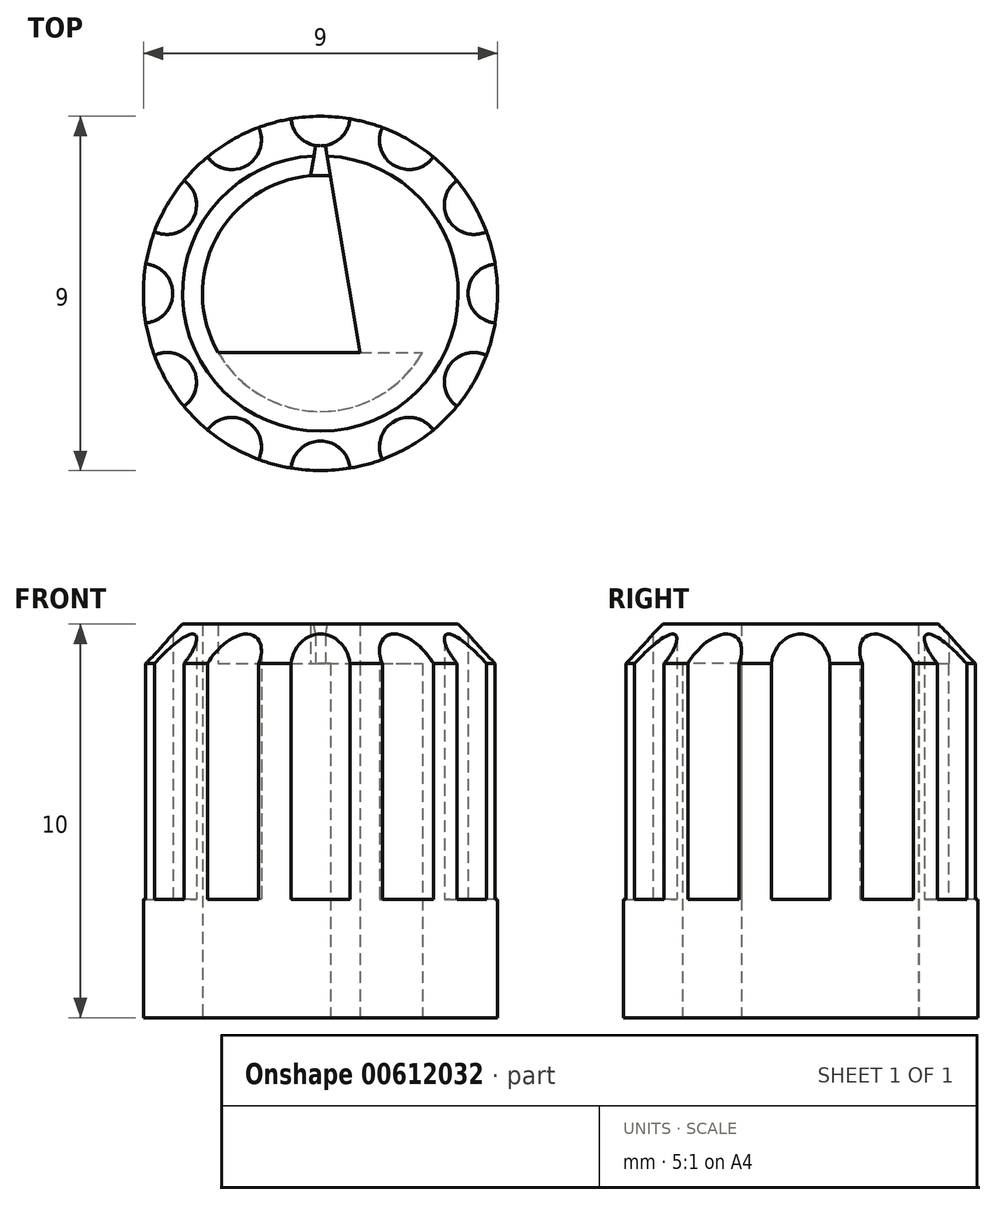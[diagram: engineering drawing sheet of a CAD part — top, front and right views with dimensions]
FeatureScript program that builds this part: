
annotation { "Feature Type Name" : "Feature", "Feature Type Description" : "" }
export const myFeature = defineFeature(function(context is Context, id is Id, definition is map)
    precondition{}
    {
        {
            var Q0;
            Q0=qCreatedBy(makeId("Top.planeOp"),FACE);
            var sketch = newSketch(context, id + "F0", { "sketchPlane" : qUnion([Q0])});
            skCircle(sketch, "E0", {"center": v(0, 0) * mm, "radius": 4.5 * mm});
            skCircle(sketch, "E1", {"center": v(0, 0) * mm, "radius": 3 * mm});
            skLineSegment(sketch, "E2", {"start": v(-2.6, -1.5) * mm, "end": v(2.6, -1.5) * mm});
            skCircle(sketch, "E3", {"center": v(0, 4.5) * mm, "radius": 0.75 * mm});
            skCircle(sketch, "E4.1.0", {"center": v(-2.25, 3.9) * mm, "radius": 0.75 * mm});
            skCircle(sketch, "E4.2.0", {"center": v(-3.9, 2.25) * mm, "radius": 0.75 * mm});
            skCircle(sketch, "E5.1.3.0", {"center": v(-4.5, 0) * mm, "radius": 0.75 * mm});
            skCircle(sketch, "E5.1.4.0", {"center": v(-3.9, -2.25) * mm, "radius": 0.75 * mm});
            skCircle(sketch, "E5.1.5.0", {"center": v(-2.25, -3.9) * mm, "radius": 0.75 * mm});
            skCircle(sketch, "E5.1.6.0", {"center": v(0, -4.5) * mm, "radius": 0.75 * mm});
            skCircle(sketch, "E5.1.7.0", {"center": v(2.25, -3.9) * mm, "radius": 0.75 * mm});
            skCircle(sketch, "E5.1.8.0", {"center": v(3.9, -2.25) * mm, "radius": 0.75 * mm});
            skCircle(sketch, "E5.1.9.0", {"center": v(4.5, 0) * mm, "radius": 0.75 * mm});
            skCircle(sketch, "E5.1.10.0", {"center": v(3.9, 2.25) * mm, "radius": 0.75 * mm});
            skCircle(sketch, "E5.1.11.0", {"center": v(2.25, 3.9) * mm, "radius": 0.75 * mm});
            skLineSegment(sketch, "E6", {"start": v(-1, -1.5) * mm, "end": v(0, 4.5) * mm});
            skLineSegment(sketch, "E7.MirrorCS", {"start": v(1, -1.5) * mm, "end": v(0, 4.5) * mm});
            skSolve(sketch);
        }
        {
            var Q0;
            {var subQ9=sQuery(id+"F0.wireOp",EDGE,"E0");var subQ29=sQuery(id+"F0.wireOp",EDGE,"E5.1.10.0");var subQ30=makeQuery(id+"F0.imprint","INTERSECT",VERTEX,{"disambiguationData":[OD(0.0)],"derivedFrom":[subQ9,subQ29]});Q0=makeQuery(id+"F0.imprint","IMPRINT",FACE,{"disambiguationData":[TD([[makeQuery(id+"F0.imprint","IMPRINT",EDGE,{"disambiguationData":[TD([[subQ30,1.0]])],"derivedFrom":subQ9}),1.0]])]});}
            var Q1;
            {var subQ0=sQuery(id+"F0.wireOp",EDGE,"E2");var subQ1=sQuery(id+"F0.wireOp",EDGE,"E1");var subQ2=makeQuery(id+"F0.imprint","INTERSECT",VERTEX,{"disambiguationData":[OD(0.0)],"derivedFrom":[subQ1,subQ0]});Q1=makeQuery(id+"F0.imprint","IMPRINT",FACE,{"disambiguationData":[TD([[makeQuery(id+"F0.imprint","IMPRINT",EDGE,{"disambiguationData":[TD([[subQ2,-1.0]])],"derivedFrom":subQ1}),1.0]])]});}
            var Q2;
            {var subQ0=sQuery(id+"F0.wireOp",EDGE,"E6");var subQ1=sQuery(id+"F0.wireOp",EDGE,"E1");var subQ2=makeQuery(id+"F0.imprint","INTERSECT",VERTEX,{"derivedFrom":[subQ1,subQ0]});Q2=makeQuery(id+"F0.imprint","IMPRINT",FACE,{"disambiguationData":[TD([[makeQuery(id+"F0.imprint","IMPRINT",EDGE,{"disambiguationData":[TD([[subQ2,1.0]])],"derivedFrom":subQ1}),-1.0]])]});}
            var Q3;
            {var subQ0=sQuery(id+"F0.wireOp",EDGE,"E6");var subQ1=sQuery(id+"F0.wireOp",EDGE,"E3");var subQ2=makeQuery(id+"F0.imprint","INTERSECT",VERTEX,{"derivedFrom":[subQ1,subQ0]});Q3=makeQuery(id+"F0.imprint","IMPRINT",FACE,{"disambiguationData":[TD([[makeQuery(id+"F0.imprint","IMPRINT",EDGE,{"disambiguationData":[TD([[subQ2,-1.0]])],"derivedFrom":subQ1}),1.0]])]});}
            var Q4;
            {var subQ1=sQuery(id+"F0.wireOp",EDGE,"E0");var subQ3=sQuery(id+"F0.wireOp",EDGE,"E3");var subQ4=makeQuery(id+"F0.imprint","INTERSECT",VERTEX,{"disambiguationData":[OD(0.0)],"derivedFrom":[subQ1,subQ3]});Q4=makeQuery(id+"F0.imprint","IMPRINT",FACE,{"disambiguationData":[TD([[makeQuery(id+"F0.imprint","IMPRINT",EDGE,{"disambiguationData":[TD([[subQ4,1.0]])],"derivedFrom":subQ3}),1.0]])]});}
            var Q5;
            {var subQ1=sQuery(id+"F0.wireOp",EDGE,"E0");var subQ3=sQuery(id+"F0.wireOp",EDGE,"E3");var subQ4=makeQuery(id+"F0.imprint","INTERSECT",VERTEX,{"disambiguationData":[OD(1.0)],"derivedFrom":[subQ1,subQ3]});Q5=makeQuery(id+"F0.imprint","IMPRINT",FACE,{"disambiguationData":[TD([[makeQuery(id+"F0.imprint","IMPRINT",EDGE,{"disambiguationData":[TD([[subQ4,-1.0]])],"derivedFrom":subQ3}),1.0]])]});}
            var Q6;
            {var subQ0=sQuery(id+"F0.wireOp",EDGE,"E5.1.11.0");var subQ1=sQuery(id+"F0.wireOp",EDGE,"E0");var subQ2=makeQuery(id+"F0.imprint","INTERSECT",VERTEX,{"disambiguationData":[OD(0.0)],"derivedFrom":[subQ1,subQ0]});Q6=makeQuery(id+"F0.imprint","IMPRINT",FACE,{"disambiguationData":[TD([[makeQuery(id+"F0.imprint","IMPRINT",EDGE,{"disambiguationData":[TD([[subQ2,-1.0]])],"derivedFrom":subQ1}),1.0]])]});}
            var Q7;
            {var subQ0=sQuery(id+"F0.wireOp",EDGE,"E5.1.10.0");var subQ1=sQuery(id+"F0.wireOp",EDGE,"E0");var subQ2=makeQuery(id+"F0.imprint","INTERSECT",VERTEX,{"disambiguationData":[OD(0.0)],"derivedFrom":[subQ1,subQ0]});Q7=makeQuery(id+"F0.imprint","IMPRINT",FACE,{"disambiguationData":[TD([[makeQuery(id+"F0.imprint","IMPRINT",EDGE,{"disambiguationData":[TD([[subQ2,-1.0]])],"derivedFrom":subQ1}),1.0]])]});}
            var Q8;
            {var subQ0=sQuery(id+"F0.wireOp",EDGE,"E5.1.9.0");var subQ1=sQuery(id+"F0.wireOp",EDGE,"E0");var subQ2=makeQuery(id+"F0.imprint","INTERSECT",VERTEX,{"disambiguationData":[OD(0.0)],"derivedFrom":[subQ1,subQ0]});Q8=makeQuery(id+"F0.imprint","IMPRINT",FACE,{"disambiguationData":[TD([[makeQuery(id+"F0.imprint","IMPRINT",EDGE,{"disambiguationData":[TD([[subQ2,1.0]])],"derivedFrom":subQ1}),1.0]])]});}
            var Q9;
            {var subQ0=sQuery(id+"F0.wireOp",EDGE,"E5.1.8.0");var subQ1=sQuery(id+"F0.wireOp",EDGE,"E0");var subQ2=makeQuery(id+"F0.imprint","INTERSECT",VERTEX,{"disambiguationData":[OD(0.0)],"derivedFrom":[subQ1,subQ0]});Q9=makeQuery(id+"F0.imprint","IMPRINT",FACE,{"disambiguationData":[TD([[makeQuery(id+"F0.imprint","IMPRINT",EDGE,{"disambiguationData":[TD([[subQ2,-1.0]])],"derivedFrom":subQ1}),1.0]])]});}
            var Q10;
            {var subQ0=sQuery(id+"F0.wireOp",EDGE,"E5.1.4.0");var subQ1=sQuery(id+"F0.wireOp",EDGE,"E0");var subQ2=makeQuery(id+"F0.imprint","INTERSECT",VERTEX,{"disambiguationData":[OD(0.0)],"derivedFrom":[subQ1,subQ0]});Q10=makeQuery(id+"F0.imprint","IMPRINT",FACE,{"disambiguationData":[TD([[makeQuery(id+"F0.imprint","IMPRINT",EDGE,{"disambiguationData":[TD([[subQ2,-1.0]])],"derivedFrom":subQ1}),1.0]])]});}
            var Q11;
            {var subQ0=sQuery(id+"F0.wireOp",EDGE,"E5.1.3.0");var subQ1=sQuery(id+"F0.wireOp",EDGE,"E0");var subQ2=makeQuery(id+"F0.imprint","INTERSECT",VERTEX,{"disambiguationData":[OD(0.0)],"derivedFrom":[subQ1,subQ0]});Q11=makeQuery(id+"F0.imprint","IMPRINT",FACE,{"disambiguationData":[TD([[makeQuery(id+"F0.imprint","IMPRINT",EDGE,{"disambiguationData":[TD([[subQ2,-1.0]])],"derivedFrom":subQ1}),1.0]])]});}
            var Q12;
            {var subQ0=sQuery(id+"F0.wireOp",EDGE,"E4.2.0");var subQ1=sQuery(id+"F0.wireOp",EDGE,"E0");var subQ2=makeQuery(id+"F0.imprint","INTERSECT",VERTEX,{"disambiguationData":[OD(0.0)],"derivedFrom":[subQ1,subQ0]});Q12=makeQuery(id+"F0.imprint","IMPRINT",FACE,{"disambiguationData":[TD([[makeQuery(id+"F0.imprint","IMPRINT",EDGE,{"disambiguationData":[TD([[subQ2,-1.0]])],"derivedFrom":subQ1}),1.0]])]});}
            var Q13;
            {var subQ0=sQuery(id+"F0.wireOp",EDGE,"E4.1.0");var subQ1=sQuery(id+"F0.wireOp",EDGE,"E0");var subQ2=makeQuery(id+"F0.imprint","INTERSECT",VERTEX,{"disambiguationData":[OD(0.0)],"derivedFrom":[subQ1,subQ0]});Q13=makeQuery(id+"F0.imprint","IMPRINT",FACE,{"disambiguationData":[TD([[makeQuery(id+"F0.imprint","IMPRINT",EDGE,{"disambiguationData":[TD([[subQ2,-1.0]])],"derivedFrom":subQ1}),1.0]])]});}
            var Q14;
            {var subQ0=sQuery(id+"F0.wireOp",EDGE,"E5.1.5.0");var subQ1=sQuery(id+"F0.wireOp",EDGE,"E0");var subQ2=makeQuery(id+"F0.imprint","INTERSECT",VERTEX,{"disambiguationData":[OD(0.0)],"derivedFrom":[subQ1,subQ0]});Q14=makeQuery(id+"F0.imprint","IMPRINT",FACE,{"disambiguationData":[TD([[makeQuery(id+"F0.imprint","IMPRINT",EDGE,{"disambiguationData":[TD([[subQ2,-1.0]])],"derivedFrom":subQ1}),1.0]])]});}
            var Q15;
            {var subQ0=sQuery(id+"F0.wireOp",EDGE,"E5.1.6.0");var subQ1=sQuery(id+"F0.wireOp",EDGE,"E0");var subQ2=makeQuery(id+"F0.imprint","INTERSECT",VERTEX,{"disambiguationData":[OD(0.0)],"derivedFrom":[subQ1,subQ0]});Q15=makeQuery(id+"F0.imprint","IMPRINT",FACE,{"disambiguationData":[TD([[makeQuery(id+"F0.imprint","IMPRINT",EDGE,{"disambiguationData":[TD([[subQ2,-1.0]])],"derivedFrom":subQ1}),1.0]])]});}
            var Q16;
            {var subQ0=sQuery(id+"F0.wireOp",EDGE,"E5.1.7.0");var subQ1=sQuery(id+"F0.wireOp",EDGE,"E0");var subQ2=makeQuery(id+"F0.imprint","INTERSECT",VERTEX,{"disambiguationData":[OD(0.0)],"derivedFrom":[subQ1,subQ0]});Q16=makeQuery(id+"F0.imprint","IMPRINT",FACE,{"disambiguationData":[TD([[makeQuery(id+"F0.imprint","IMPRINT",EDGE,{"disambiguationData":[TD([[subQ2,-1.0]])],"derivedFrom":subQ1}),1.0]])]});}
            extrude(context, id + "F1", {"entities" : qUnion([Q0, Q1, Q2, Q3, Q4, Q5, Q6, Q7, Q8, Q9, Q10, Q11, Q12, Q13, Q14, Q15, Q16]), "depth" : 3 * mm, "offsetDistance" : 25 * mm});
        }
        {
            var Q0;
            {var subQ9=sQuery(id+"F0.wireOp",EDGE,"E0");var subQ29=sQuery(id+"F0.wireOp",EDGE,"E5.1.10.0");var subQ30=makeQuery(id+"F0.imprint","INTERSECT",VERTEX,{"disambiguationData":[OD(0.0)],"derivedFrom":[subQ9,subQ29]});Q0=makeQuery(id+"F0.imprint","IMPRINT",FACE,{"disambiguationData":[TD([[makeQuery(id+"F0.imprint","IMPRINT",EDGE,{"disambiguationData":[TD([[subQ30,1.0]])],"derivedFrom":subQ9}),1.0]])]});}
            var Q1;
            {var subQ0=sQuery(id+"F0.wireOp",EDGE,"E6");var subQ1=sQuery(id+"F0.wireOp",EDGE,"E1");var subQ2=makeQuery(id+"F0.imprint","INTERSECT",VERTEX,{"derivedFrom":[subQ1,subQ0]});Q1=makeQuery(id+"F0.imprint","IMPRINT",FACE,{"disambiguationData":[TD([[makeQuery(id+"F0.imprint","IMPRINT",EDGE,{"disambiguationData":[TD([[subQ2,1.0]])],"derivedFrom":subQ1}),-1.0]])]});}
            var Q2;
            {var subQ0=sQuery(id+"F0.wireOp",EDGE,"E2");var subQ1=sQuery(id+"F0.wireOp",EDGE,"E1");var subQ2=makeQuery(id+"F0.imprint","INTERSECT",VERTEX,{"disambiguationData":[OD(0.0)],"derivedFrom":[subQ1,subQ0]});Q2=makeQuery(id+"F0.imprint","IMPRINT",FACE,{"disambiguationData":[TD([[makeQuery(id+"F0.imprint","IMPRINT",EDGE,{"disambiguationData":[TD([[subQ2,-1.0]])],"derivedFrom":subQ1}),1.0]])]});}
            extrude(context, id + "F2", {"entities" : qUnion([Q0, Q1, Q2]), "operationType" : NewBodyOperationType.ADD, "depth" : 9 * mm, "offsetDistance" : 25 * mm});
        }
        {
            var Q0;
            {var subQ9=sQuery(id+"F0.wireOp",EDGE,"E0");var subQ29=sQuery(id+"F0.wireOp",EDGE,"E5.1.10.0");var subQ30=makeQuery(id+"F0.imprint","INTERSECT",VERTEX,{"disambiguationData":[OD(0.0)],"derivedFrom":[subQ9,subQ29]});Q0=makeQuery(id+"F0.imprint","IMPRINT",FACE,{"disambiguationData":[TD([[makeQuery(id+"F0.imprint","IMPRINT",EDGE,{"disambiguationData":[TD([[subQ30,1.0]])],"derivedFrom":subQ9}),1.0]])]});}
            var Q1;
            {var subQ0=sQuery(id+"F0.wireOp",EDGE,"E2");var subQ1=sQuery(id+"F0.wireOp",EDGE,"E1");var subQ2=makeQuery(id+"F0.imprint","INTERSECT",VERTEX,{"disambiguationData":[OD(0.0)],"derivedFrom":[subQ1,subQ0]});Q1=makeQuery(id+"F0.imprint","IMPRINT",FACE,{"disambiguationData":[TD([[makeQuery(id+"F0.imprint","IMPRINT",EDGE,{"disambiguationData":[TD([[subQ2,-1.0]])],"derivedFrom":subQ1}),1.0]])]});}
            var Q2;
            {var subQ0=sQuery(id+"F0.wireOp",EDGE,"E2");var subQ1=sQuery(id+"F0.wireOp",EDGE,"E1");var subQ2=makeQuery(id+"F0.imprint","INTERSECT",VERTEX,{"disambiguationData":[OD(0.0)],"derivedFrom":[subQ1,subQ0]});Q2=makeQuery(id+"F0.imprint","IMPRINT",FACE,{"disambiguationData":[TD([[makeQuery(id+"F0.imprint","IMPRINT",EDGE,{"disambiguationData":[TD([[subQ2,1.0]])],"derivedFrom":subQ1}),1.0]])]});}
            var Q3;
            {var subQ0=sQuery(id+"F0.wireOp",EDGE,"E2");var subQ1=sQuery(id+"F0.wireOp",EDGE,"E1");var subQ2=makeQuery(id+"F0.imprint","INTERSECT",VERTEX,{"disambiguationData":[OD(1.0)],"derivedFrom":[subQ1,subQ0]});Q3=makeQuery(id+"F0.imprint","IMPRINT",FACE,{"disambiguationData":[TD([[makeQuery(id+"F0.imprint","IMPRINT",EDGE,{"disambiguationData":[TD([[subQ2,-1.0]])],"derivedFrom":subQ1}),1.0]])]});}
            extrude(context, id + "F3", {"entities" : qUnion([Q0, Q1, Q2, Q3]), "operationType" : NewBodyOperationType.ADD, "depth" : 10 * mm, "offsetDistance" : 25 * mm, "hasSecondDirection" : true, "secondDirectionOppositeDirection" : false, "secondDirectionDepth" : 9 * mm});
        }
        {
            var Q0;
            {var subQ0=sQuery(id+"F0.wireOp",EDGE,"E0");Q0=makeQuery(id+"F3.opExtrude","CAP_EDGE",EDGE,{"disambiguationData":[OSD([subQ0]),TDD([makeQuery(id+"F0.imprint","IMPRINT",EDGE,{"disambiguationData":[TD([[makeQuery(id+"F0.imprint","INTERSECT",VERTEX,{"disambiguationData":[OD(1.0)],"derivedFrom":[subQ0,sQuery(id+"F0.wireOp",EDGE,"E5.1.6.0")]}),-1.0]])],"derivedFrom":subQ0})])],"isStart":false});}
            var Q1;
            {var subQ0=sQuery(id+"F0.wireOp",EDGE,"E0");Q1=makeQuery(id+"F3.opExtrude","CAP_EDGE",EDGE,{"disambiguationData":[OSD([subQ0]),TDD([makeQuery(id+"F0.imprint","IMPRINT",EDGE,{"disambiguationData":[TD([[makeQuery(id+"F0.imprint","INTERSECT",VERTEX,{"disambiguationData":[OD(1.0)],"derivedFrom":[subQ0,sQuery(id+"F0.wireOp",EDGE,"E5.1.7.0")]}),-1.0]])],"derivedFrom":subQ0})])],"isStart":false});}
            var Q2;
            {var subQ0=sQuery(id+"F0.wireOp",EDGE,"E0");Q2=makeQuery(id+"F3.opExtrude","CAP_EDGE",EDGE,{"disambiguationData":[OSD([subQ0]),TDD([makeQuery(id+"F0.imprint","IMPRINT",EDGE,{"disambiguationData":[TD([[makeQuery(id+"F0.imprint","INTERSECT",VERTEX,{"disambiguationData":[OD(1.0)],"derivedFrom":[subQ0,sQuery(id+"F0.wireOp",EDGE,"E5.1.8.0")]}),-1.0]])],"derivedFrom":subQ0})])],"isStart":false});}
            var Q3;
            {var subQ0=sQuery(id+"F0.wireOp",EDGE,"E0");Q3=makeQuery(id+"F3.opExtrude","CAP_EDGE",EDGE,{"disambiguationData":[OSD([subQ0]),TDD([makeQuery(id+"F0.imprint","IMPRINT",EDGE,{"disambiguationData":[TD([[makeQuery(id+"F0.imprint","INTERSECT",VERTEX,{"disambiguationData":[OD(0.0)],"derivedFrom":[subQ0,sQuery(id+"F0.wireOp",EDGE,"E5.1.10.0")]}),1.0]])],"derivedFrom":subQ0})])],"isStart":false});}
            var Q4;
            {var subQ0=sQuery(id+"F0.wireOp",EDGE,"E0");Q4=makeQuery(id+"F3.opExtrude","CAP_EDGE",EDGE,{"disambiguationData":[OSD([subQ0]),TDD([makeQuery(id+"F0.imprint","IMPRINT",EDGE,{"disambiguationData":[TD([[makeQuery(id+"F0.imprint","INTERSECT",VERTEX,{"disambiguationData":[OD(1.0)],"derivedFrom":[subQ0,sQuery(id+"F0.wireOp",EDGE,"E5.1.10.0")]}),-1.0]])],"derivedFrom":subQ0})])],"isStart":false});}
            var Q5;
            {var subQ0=sQuery(id+"F0.wireOp",EDGE,"E0");Q5=makeQuery(id+"F3.opExtrude","CAP_EDGE",EDGE,{"disambiguationData":[OSD([subQ0]),TDD([makeQuery(id+"F0.imprint","IMPRINT",EDGE,{"disambiguationData":[TD([[makeQuery(id+"F0.imprint","INTERSECT",VERTEX,{"disambiguationData":[OD(1.0)],"derivedFrom":[subQ0,sQuery(id+"F0.wireOp",EDGE,"E5.1.11.0")]}),-1.0]])],"derivedFrom":subQ0})])],"isStart":false});}
            var Q6;
            {var subQ0=sQuery(id+"F0.wireOp",EDGE,"E0");Q6=makeQuery(id+"F3.opExtrude","CAP_EDGE",EDGE,{"disambiguationData":[OSD([subQ0]),TDD([makeQuery(id+"F0.imprint","IMPRINT",EDGE,{"disambiguationData":[TD([[makeQuery(id+"F0.imprint","INTERSECT",VERTEX,{"disambiguationData":[OD(1.0)],"derivedFrom":[subQ0,sQuery(id+"F0.wireOp",EDGE,"E5.1.5.0")]}),-1.0]])],"derivedFrom":subQ0})])],"isStart":false});}
            var Q7;
            {var subQ0=sQuery(id+"F0.wireOp",EDGE,"E0");Q7=makeQuery(id+"F3.opExtrude","CAP_EDGE",EDGE,{"disambiguationData":[OSD([subQ0]),TDD([makeQuery(id+"F0.imprint","IMPRINT",EDGE,{"disambiguationData":[TD([[makeQuery(id+"F0.imprint","INTERSECT",VERTEX,{"disambiguationData":[OD(1.0)],"derivedFrom":[subQ0,sQuery(id+"F0.wireOp",EDGE,"E5.1.4.0")]}),-1.0]])],"derivedFrom":subQ0})])],"isStart":false});}
            var Q8;
            {var subQ0=sQuery(id+"F0.wireOp",EDGE,"E0");Q8=makeQuery(id+"F3.opExtrude","CAP_EDGE",EDGE,{"disambiguationData":[OSD([subQ0]),TDD([makeQuery(id+"F0.imprint","IMPRINT",EDGE,{"disambiguationData":[TD([[makeQuery(id+"F0.imprint","INTERSECT",VERTEX,{"disambiguationData":[OD(1.0)],"derivedFrom":[subQ0,sQuery(id+"F0.wireOp",EDGE,"E5.1.3.0")]}),-1.0]])],"derivedFrom":subQ0})])],"isStart":false});}
            var Q9;
            {var subQ0=sQuery(id+"F0.wireOp",EDGE,"E0");Q9=makeQuery(id+"F3.opExtrude","CAP_EDGE",EDGE,{"disambiguationData":[OSD([subQ0]),TDD([makeQuery(id+"F0.imprint","IMPRINT",EDGE,{"disambiguationData":[TD([[makeQuery(id+"F0.imprint","INTERSECT",VERTEX,{"disambiguationData":[OD(1.0)],"derivedFrom":[subQ0,sQuery(id+"F0.wireOp",EDGE,"E4.2.0")]}),-1.0]])],"derivedFrom":subQ0})])],"isStart":false});}
            var Q10;
            {var subQ0=sQuery(id+"F0.wireOp",EDGE,"E0");Q10=makeQuery(id+"F3.opExtrude","CAP_EDGE",EDGE,{"disambiguationData":[OSD([subQ0]),TDD([makeQuery(id+"F0.imprint","IMPRINT",EDGE,{"disambiguationData":[TD([[makeQuery(id+"F0.imprint","INTERSECT",VERTEX,{"disambiguationData":[OD(1.0)],"derivedFrom":[subQ0,sQuery(id+"F0.wireOp",EDGE,"E4.1.0")]}),-1.0]])],"derivedFrom":subQ0})])],"isStart":false});}
            var Q11;
            {var subQ0=sQuery(id+"F0.wireOp",EDGE,"E0");Q11=makeQuery(id+"F3.opExtrude","CAP_EDGE",EDGE,{"disambiguationData":[OSD([subQ0]),TDD([makeQuery(id+"F0.imprint","IMPRINT",EDGE,{"disambiguationData":[TD([[makeQuery(id+"F0.imprint","INTERSECT",VERTEX,{"disambiguationData":[OD(1.0)],"derivedFrom":[subQ0,sQuery(id+"F0.wireOp",EDGE,"E3")]}),-1.0]])],"derivedFrom":subQ0})])],"isStart":false});}
            chamfer(context, id + "F4", {"entities" : qUnion([Q0, Q1, Q2, Q3, Q4, Q5, Q6, Q7, Q8, Q9, Q10, Q11]), "width" : 1 * mm, "tangentPropagation" : true});
        }
    });
